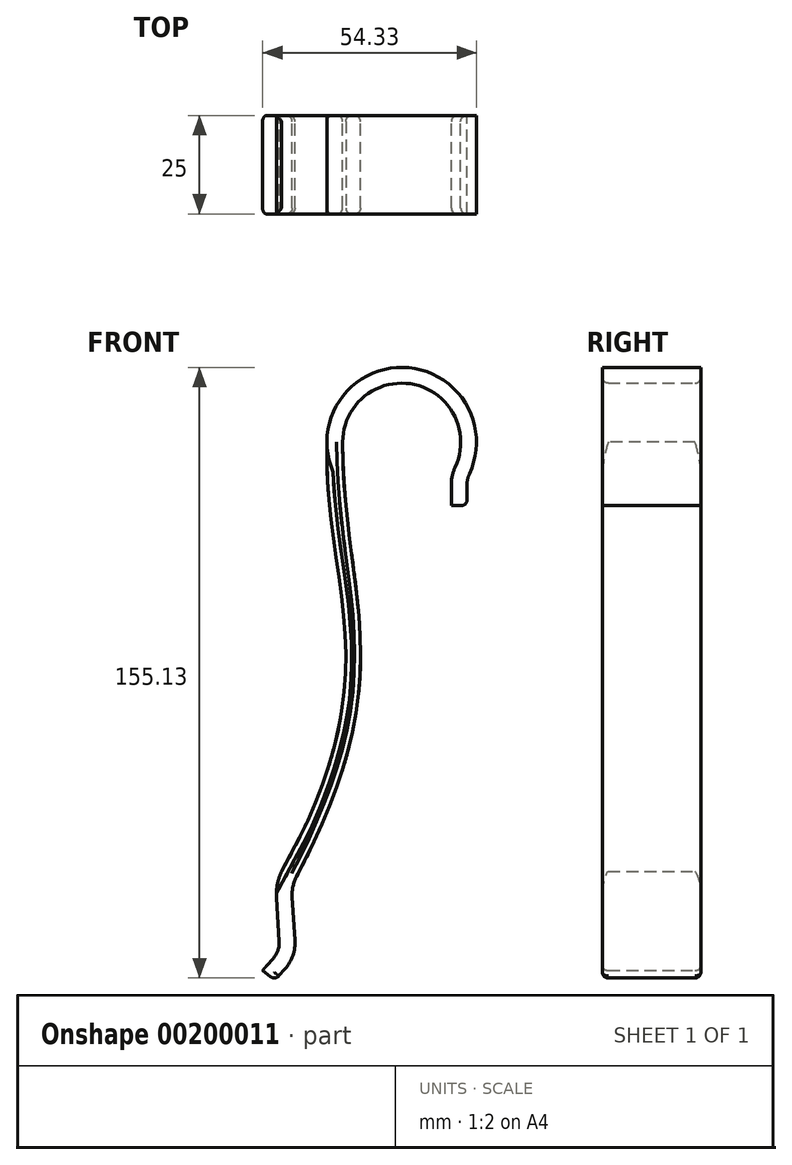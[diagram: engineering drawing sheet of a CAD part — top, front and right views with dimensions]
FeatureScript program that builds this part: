
annotation { "Feature Type Name" : "Feature", "Feature Type Description" : "" }
export const myFeature = defineFeature(function(context is Context, id is Id, definition is map)
    precondition{}
    {
        {
            var Q0;
            Q0=qCreatedBy(makeId("Front.planeOp"),FACE);
            var sketch = newSketch(context, id + "F0", { "sketchPlane" : qUnion([Q0])});
            skLineSegment(sketch, "E0", {"start": v(-209.6, -12.92) * mm, "end": v(-4, -0.25) * mm, "construction": true});
            skLineSegment(sketch, "E1", {"start": v(0.25, -4) * mm, "end": v(0.86, -13.97) * mm, "construction": true});
            skLineSegment(sketch, "E2", {"start": v(-2.88, -18.21) * mm, "end": v(-95.14, -23.9) * mm, "construction": true});
            skPoint(sketch, "E3.visualSharp", {"position": v(0, 0) * mm});
            skArc(sketch, "E3.filletArc", {"start": v(0.25, -4) * mm, "mid": v(-1.1, -1.24) * mm, "end": v(-4, -0.25) * mm, "construction": true});
            skPoint(sketch, "E4.visualSharp", {"position": v(1.1, -17.97) * mm});
            skArc(sketch, "E4.filletArc", {"start": v(-2.88, -18.21) * mm, "mid": v(-0.13, -16.87) * mm, "end": v(0.86, -13.97) * mm, "construction": true});
            skLineSegment(sketch, "E5", {"start": v(-7.98, -0.5) * mm, "end": v(-6.88, -18.46) * mm, "construction": true});
            skLineSegment(sketch, "E6", {"start": v(-14.97, -0.92) * mm, "end": v(-13.86, -18.89) * mm, "construction": true});
            skLineSegment(sketch, "E7", {"start": v(0, 0) * mm, "end": v(0, 112.23) * mm, "construction": true});
            skLineSegment(sketch, "E8", {"start": v(0, 112.23) * mm, "end": v(20, 112.23) * mm, "construction": true});
            skCircle(sketch, "E9", {"center": v(20, 112.23) * mm, "radius": 15 * mm, "construction": true});
            skSolve(sketch);
        }
        {
            var Q0;
            Q0=qCreatedBy(makeId("Front.planeOp"),FACE);
            var sketch = newSketch(context, id + "F1", { "sketchPlane" : qUnion([Q0])});
            skLineSegment(sketch, "E10", {"start": v(-7.13, -14.32) * mm, "end": v(-7.8, -3.34) * mm});
            skArc(sketch, "E11", {"start": v(5, 112.23) * mm, "mid": v(23.28, 126.87) * mm, "end": v(33.56, 105.83) * mm});
            skLineSegment(sketch, "E12", {"start": v(32.6, 101.56) * mm, "end": v(32.6, 96.1) * mm});
            skLineSegment(sketch, "E13", {"start": v(-9.62, -21.56) * mm, "end": v(-12.18, -24.45) * mm});
            skFitSpline(sketch, "E14", {"points": [v(-7.98, -0.5) * mm, v(5, 112.23) * mm], "startDerivative": vector(88.06, 161.26) * mm, "endDerivative": vector(-0.07, 121.41) * mm});
            skArc(sketch, "E15.filletArc", {"start": v(-6.66, 1.97) * mm, "mid": v(-7.6, -0.6) * mm, "end": v(-7.8, -3.34) * mm});
            skPoint(sketch, "E16.visualSharp", {"position": v(-6.88, -18.46) * mm});
            skArc(sketch, "E16.filletArc", {"start": v(-9.62, -21.56) * mm, "mid": v(-7.66, -18.2) * mm, "end": v(-7.13, -14.32) * mm});
            skPoint(sketch, "E17.visualSharp", {"position": v(32.6, 104.1) * mm});
            skArc(sketch, "E17.filletArc", {"start": v(33.56, 105.83) * mm, "mid": v(32.85, 103.75) * mm, "end": v(32.6, 101.56) * mm});
            skLineSegment(sketch, "E18.0", {"start": v(36.6, 101.56) * mm, "end": v(36.6, 96.1) * mm});
            skArc(sketch, "E18.1", {"start": v(37.18, 104.12) * mm, "mid": v(36.75, 102.87) * mm, "end": v(36.6, 101.56) * mm});
            skArc(sketch, "E18.2", {"start": v(1, 112.23) * mm, "mid": v(24.15, 130.77) * mm, "end": v(37.18, 104.12) * mm});
            skFitSpline(sketch, "E18.3", {"points": [v(-11.5, 1.42) * mm, v(-7.89, 8.03) * mm, v(-2.1, 20.1) * mm, v(3.02, 35.46) * mm, v(5.39, 48.76) * mm, v(5.75, 60.82) * mm, v(4.78, 72.46) * mm, v(3.14, 84.43) * mm, v(1.53, 97.36) * mm, v(1, 107.04) * mm, v(1, 112.23) * mm]});
            skLineSegment(sketch, "E18.4", {"start": v(-12.62, -18.91) * mm, "end": v(-15.33, -21.99) * mm});
            skArc(sketch, "E18.5", {"start": v(-12.62, -18.91) * mm, "mid": v(-11.44, -16.89) * mm, "end": v(-11.12, -14.57) * mm});
            skLineSegment(sketch, "E18.6", {"start": v(-11.12, -14.57) * mm, "end": v(-11.8, -3.58) * mm});
            skArc(sketch, "E18.7", {"start": v(-10.2, 3.84) * mm, "mid": v(-11.51, 0.24) * mm, "end": v(-11.8, -3.58) * mm});
            skLineSegment(sketch, "E19", {"start": v(32.6, 96.1) * mm, "end": v(36.6, 96.1) * mm});
            skLineSegment(sketch, "E20", {"start": v(-12.18, -24.45) * mm, "end": v(-15.33, -21.99) * mm});
            skSolve(sketch);
        }
        {
            var Q0;
            Q0 = qSketchRegion(id + "F1", true);
            extrude(context, id + "F2", {"entities" : qUnion([Q0]), "endBound" : BoundingType.SYMMETRIC, "depth" : 25 * mm});
        }
        {
            var Q0;
            Q0=makeQuery(id+"F2.opExtrude","CAP_EDGE",EDGE,{"disambiguationData":[OSD([sQuery(id+"F1.wireOp",EDGE,"E14")])],"isStart":false});
            var Q1;
            Q1=makeQuery(id+"F2.opExtrude","CAP_EDGE",EDGE,{"disambiguationData":[OSD([sQuery(id+"F1.wireOp",EDGE,"E18.3")])],"isStart":false});
            var Q2;
            Q2=makeQuery(id+"F2.opExtrude","CAP_EDGE",EDGE,{"disambiguationData":[OSD([sQuery(id+"F1.wireOp",EDGE,"E18.3")])],"isStart":true});
            var Q3;
            Q3=makeQuery(id+"F2.opExtrude","CAP_EDGE",EDGE,{"disambiguationData":[OSD([sQuery(id+"F1.wireOp",EDGE,"E14")])],"isStart":true});
            fillet(context, id + "F3", {"entities" : qUnion([Q0, Q1, Q2, Q3]), "radius" : 1.5 * mm, "tangentPropagation" : true, "allowEdgeOverflow" : false});
        }
        {
            var Q0;
            Q0=makeQuery(id+"F2.opExtrude","SWEPT_EDGE",EDGE,{"disambiguationData":[OSD([sQuery(id+"F1.wireOp",EDGE,"E18.0"),sQuery(id+"F1.wireOp",EDGE,"E19")])]});
            var Q1;
            Q1=makeQuery(id+"F2.opExtrude","SWEPT_EDGE",EDGE,{"disambiguationData":[OSD([sQuery(id+"F1.wireOp",EDGE,"E13"),sQuery(id+"F1.wireOp",EDGE,"E20")])]});
            fillet(context, id + "F4", {"entities" : qUnion([Q0, Q1]), "radius" : 1.5 * mm, "tangentPropagation" : true, "allowEdgeOverflow" : false});
        }
    });
